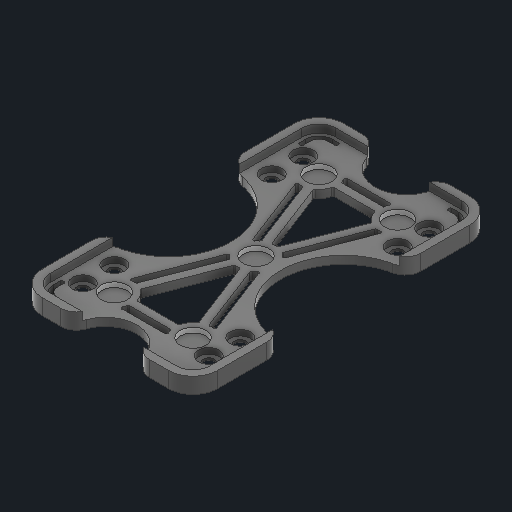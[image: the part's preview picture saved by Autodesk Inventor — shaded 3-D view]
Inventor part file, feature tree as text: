
AUTODESK INVENTOR PART (.ipt)
format: ipt  version: 2025 (Build 290162000, 162)  size: 394,752 bytes
history: native  units: in
note: dims shown in document units (in); Inventor stores cm internally (conversion verified against a paired STEP export)
features: projected_geometry x5, extrude x1, sketch x1
ambient origin geometry x8: Origin, YZ Plane, XZ Plane, XY Plane, X Axis, Y Axis, Z Axis, Center Point
bodies: Solid2 (feature_tree), Solid1 (feature_tree)
feature tree (7):
  extrude  "Extrusion1"  Depth=0.5in
  sketch  "Sketch1"  dims[d5=0.0787in d6=0.0in d7=0.007in d8=0.007in d9=0.007in d10=0.007in d11=0.007in d12=0.5in d13=1.9685in d14=0.5in d15=1.9685in]
  projected_geometry  "Projected Loop5"
  projected_geometry  "Projected Loop6"
  projected_geometry  "Projected Loop7"
  projected_geometry  "Projected Loop8"
  projected_geometry  "Projected Loop9"
